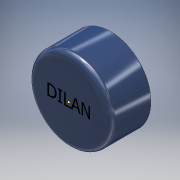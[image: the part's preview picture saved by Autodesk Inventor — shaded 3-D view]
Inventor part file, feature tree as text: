
AUTODESK INVENTOR PART (.ipt)
format: ipt  version: 2018 (Build 220112000, 112)  size: 153,600 bytes
history: native  units: mm
features: sketch x4, extrude x2, fillet x2, thread x1
ambient origin geometry x8: Origin, YZ Plane, XZ Plane, XY Plane, X Axis, Y Axis, Z Axis, Center Point
bodies: Solid1 (feature_tree)
feature tree (9):
  extrude  "Extrusion1"  Depth=11.0mm TaperAngle=0.0deg
  extrude  "Extrusion2"  Depth=10.0mm TaperAngle=0.0deg
  fillet  "Fillet1"  Radius=1.5mm
  fillet  "Fillet2"  Radius=0.25mm
  thread  "Thread1"  [1 undecoded]
  sketch  "Sketch3"
  sketch  "Sketch4"
  sketch  "Sketch1"  dims[d0=21.5mm d1=11.0mm d2=0.0mm]
  sketch  "Sketch2"  dims[d3=20.0mm d4=10.0mm d5=0.0mm d6=1.5mm d7=0.25mm d8=10.0mm d9=0.0mm]
note: 1 required parameter value undecoded (feature->parameter linkage not recoverable at this tier; creation-order binding heuristic only, values carry confidence <= 0.55)
